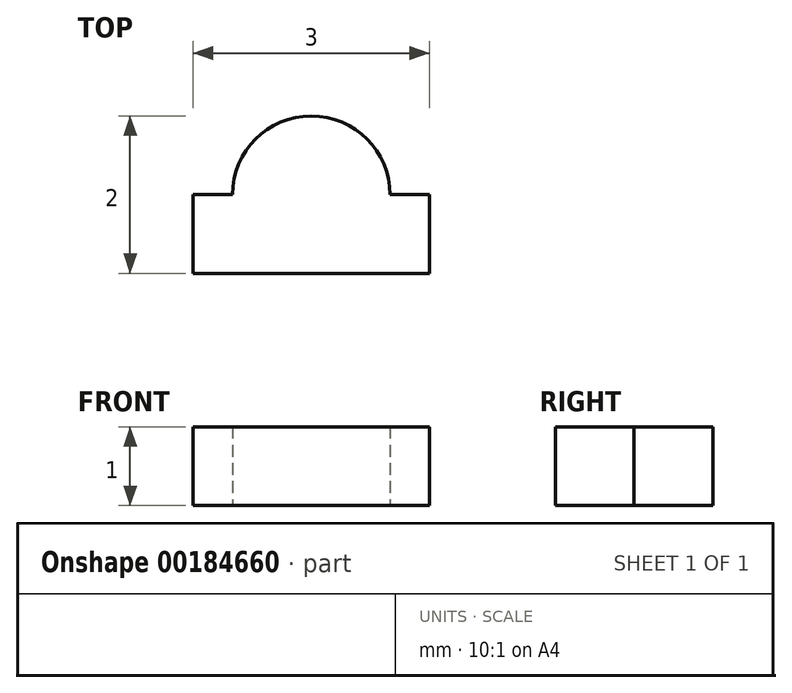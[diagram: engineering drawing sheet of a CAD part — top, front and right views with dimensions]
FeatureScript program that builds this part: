
annotation { "Feature Type Name" : "Feature", "Feature Type Description" : "" }
export const myFeature = defineFeature(function(context is Context, id is Id, definition is map)
    precondition{}
    {
        {
            var Q0;
            Q0=qCreatedBy(makeId("Top.planeOp"),FACE);
            var sketch = newSketch(context, id + "F0", { "sketchPlane" : qUnion([Q0])});
            skLineSegment(sketch, "E0", {"start": v(0, 0) * mm, "end": v(-1.5, 0) * mm});
            skLineSegment(sketch, "E1", {"start": v(-1.5, 0) * mm, "end": v(-1.5, 1) * mm});
            skLineSegment(sketch, "E2", {"start": v(-1.5, 1) * mm, "end": v(-1, 1) * mm});
            skLineSegment(sketch, "E3", {"start": v(0, 0) * mm, "end": v(0, 2) * mm});
            skArc(sketch, "E4", {"start": v(0, 2) * mm, "mid": v(-0.7, 1.7) * mm, "end": v(-1, 1) * mm});
            skSolve(sketch);
        }
        {
            var Q0;
            Q0 = qSketchRegion(id + "F0", true);
            extrude(context, id + "F1", {"entities" : qUnion([Q0]), "depth" : 1 * mm, "offsetDistance" : 25 * mm});
        }
        {
            var Q0;
            Q0=makeQuery(id+"F1.opExtrude","SWEPT_BODY",BODY,{"disambiguationData":[OSD([sQuery(id+"F0.wireOp",EDGE,"E0"),sQuery(id+"F0.wireOp",EDGE,"E1"),sQuery(id+"F0.wireOp",EDGE,"E2"),sQuery(id+"F0.wireOp",EDGE,"E3"),sQuery(id+"F0.wireOp",EDGE,"E4")])]});
            var Q1;
            Q1=makeQuery(id+"F1.opExtrude","SWEPT_FACE",FACE,{"disambiguationData":[OSD([sQuery(id+"F0.wireOp",EDGE,"E3")])]});
            mirror(context, id + "F2", {"operationType" : NewBodyOperationType.ADD, "entities" : qUnion([Q0]), "mirrorPlane" : qUnion([Q1])});
        }
    });
